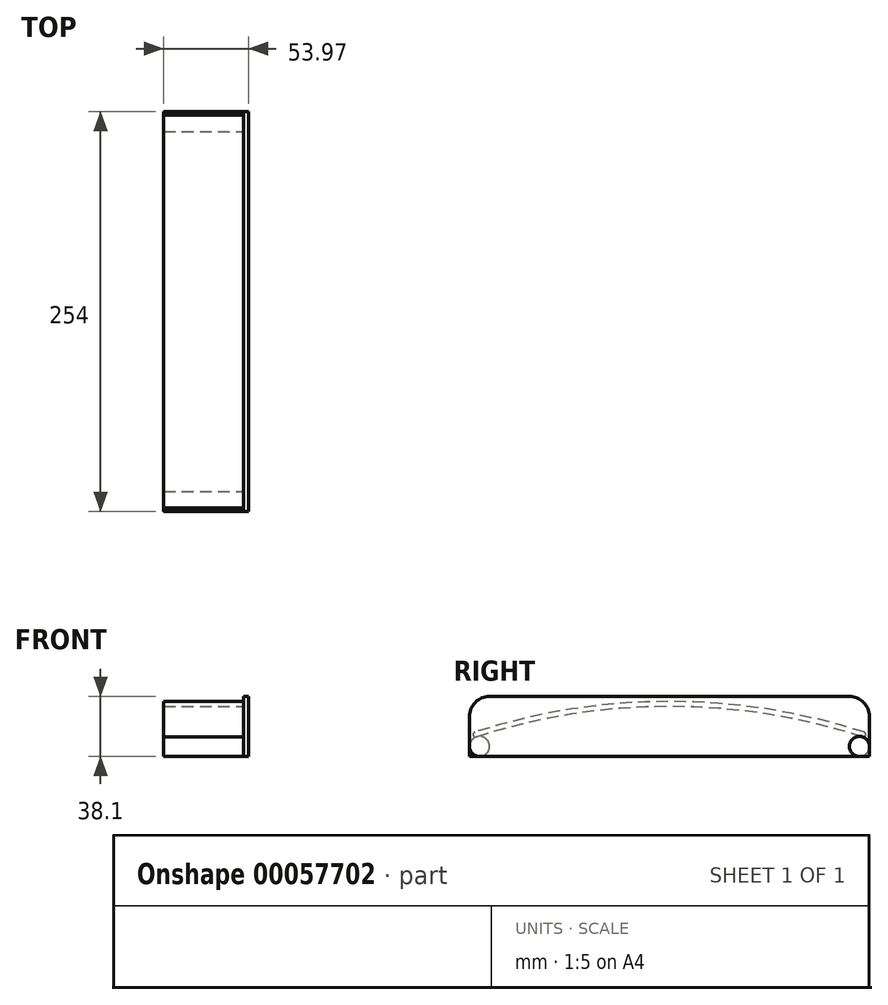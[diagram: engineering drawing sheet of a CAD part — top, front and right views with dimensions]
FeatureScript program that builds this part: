
annotation { "Feature Type Name" : "Feature", "Feature Type Description" : "" }
export const myFeature = defineFeature(function(context is Context, id is Id, definition is map)
    precondition{}
    {
        {
            var Q0;
            Q0=qCreatedBy(makeId("Right.planeOp"),FACE);
            var sketch = newSketch(context, id + "F0", { "sketchPlane" : qUnion([Q0])});
            skLineSegment(sketch, "E0.rect.bottom", {"start": v(-114.3, 19.05) * mm, "end": v(114.3, 19.05) * mm});
            skLineSegment(sketch, "E0.rect.top", {"start": v(-127, -19.05) * mm, "end": v(127, -19.05) * mm});
            skLineSegment(sketch, "E0.rect.left", {"start": v(-127, 6.35) * mm, "end": v(-127, -19.05) * mm});
            skLineSegment(sketch, "E0.rect.right", {"start": v(127, 6.35) * mm, "end": v(127, -19.05) * mm});
            skPoint(sketch, "E0.rect.middle", {"position": v(0, 0) * mm});
            skCircle(sketch, "E1", {"center": v(-120.65, -12.7) * mm, "radius": 6.35 * mm});
            skCircle(sketch, "E2", {"center": v(120.65, -12.7) * mm, "radius": 6.35 * mm});
            skPoint(sketch, "E3.visualSharp", {"position": v(-127, 19.05) * mm});
            skArc(sketch, "E3.filletArc", {"start": v(-114.3, 19.05) * mm, "mid": v(-123.28, 15.33) * mm, "end": v(-127, 6.35) * mm});
            skPoint(sketch, "E4.visualSharp", {"position": v(127, 19.05) * mm});
            skArc(sketch, "E4.filletArc", {"start": v(127, 6.35) * mm, "mid": v(123.28, 15.33) * mm, "end": v(114.3, 19.05) * mm});
            skArc(sketch, "E5", {"start": v(122.6, -6.66) * mm, "mid": v(0, 12.7) * mm, "end": v(-122.6, -6.66) * mm});
            skArc(sketch, "E6.0", {"start": v(123.58, -3.64) * mm, "mid": v(0, 15.87) * mm, "end": v(-123.58, -3.64) * mm});
            skArc(sketch, "E7", {"start": v(-123.58, -3.64) * mm, "mid": v(-124.6, -5.64) * mm, "end": v(-122.6, -6.66) * mm});
            skArc(sketch, "E8", {"start": v(122.6, -6.66) * mm, "mid": v(124.6, -5.64) * mm, "end": v(123.58, -3.64) * mm});
            skSolve(sketch);
        }
        {
            var Q0;
            {var subQ5=sQuery(id+"F0.wireOp",EDGE,"E5");Q0=makeQuery(id+"F0.imprint","IMPRINT",FACE,{"disambiguationData":[TD([[makeQuery(id+"F0.imprint","IMPRINT",EDGE,{"derivedFrom":subQ5}),1.0]])]});}
            var Q1;
            Q1=makeQuery(id+"F0.imprint","IMPRINT",FACE,{"disambiguationData":[TD([[makeQuery(id+"F0.imprint","IMPRINT",EDGE,{"derivedFrom":sQuery(id+"F0.wireOp",EDGE,"E5")}),-1.0]])]});
            var Q2;
            {var subQ0=sQuery(id+"F0.wireOp",EDGE,"E0.rect.left");var subQ1=sQuery(id+"F0.wireOp",EDGE,"E0.rect.top");var subQ2=makeQuery(id+"F0.imprint","INTERSECT",VERTEX,{"derivedFrom":[subQ1,subQ0]});Q2=makeQuery(id+"F0.imprint","IMPRINT",FACE,{"disambiguationData":[TD([[makeQuery(id+"F0.imprint","IMPRINT",EDGE,{"disambiguationData":[TD([[subQ2,-1.0]])],"derivedFrom":subQ1}),1.0]])]});}
            var Q3;
            Q3=makeQuery(id+"F0.imprint","IMPRINT",FACE,{"disambiguationData":[TD([[makeQuery(id+"F0.imprint","IMPRINT",EDGE,{"derivedFrom":sQuery(id+"F0.wireOp",EDGE,"E0.rect.bottom")}),-1.0]])]});
            var Q4;
            {var subQ0=sQuery(id+"F0.wireOp",EDGE,"E0.rect.right");var subQ1=sQuery(id+"F0.wireOp",EDGE,"E0.rect.top");var subQ2=makeQuery(id+"F0.imprint","INTERSECT",VERTEX,{"derivedFrom":[subQ1,subQ0]});Q4=makeQuery(id+"F0.imprint","IMPRINT",FACE,{"disambiguationData":[TD([[makeQuery(id+"F0.imprint","IMPRINT",EDGE,{"disambiguationData":[TD([[subQ2,1.0]])],"derivedFrom":subQ1}),1.0]])]});}
            var Q5;
            {var subQ0=sQuery(id+"F0.wireOp",EDGE,"E1");var subQ3=makeQuery(id+"F0.imprint","INTERSECT",VERTEX,{"derivedFrom":[sQuery(id+"F0.wireOp",EDGE,"E0.rect.top"),subQ0]});Q5=makeQuery(id+"F0.imprint","IMPRINT",FACE,{"disambiguationData":[TD([[makeQuery(id+"F0.imprint","IMPRINT",EDGE,{"disambiguationData":[TD([[subQ3,1.0]])],"derivedFrom":subQ0}),1.0]])]});}
            var Q6;
            {var subQ0=sQuery(id+"F0.wireOp",EDGE,"E2");var subQ3=makeQuery(id+"F0.imprint","INTERSECT",VERTEX,{"derivedFrom":[sQuery(id+"F0.wireOp",EDGE,"E0.rect.top"),subQ0]});Q6=makeQuery(id+"F0.imprint","IMPRINT",FACE,{"disambiguationData":[TD([[makeQuery(id+"F0.imprint","IMPRINT",EDGE,{"disambiguationData":[TD([[subQ3,-1.0]])],"derivedFrom":subQ0}),1.0]])]});}
            extrude(context, id + "F1", {"entities" : qUnion([Q0, Q1, Q2, Q3, Q4, Q5, Q6]), "depth" : 3.17 * mm});
        }
        {
            var Q0;
            {var subQ0=sQuery(id+"F0.wireOp",EDGE,"E1");var subQ3=makeQuery(id+"F0.imprint","INTERSECT",VERTEX,{"derivedFrom":[sQuery(id+"F0.wireOp",EDGE,"E0.rect.top"),subQ0]});Q0=makeQuery(id+"F0.imprint","IMPRINT",FACE,{"disambiguationData":[TD([[makeQuery(id+"F0.imprint","IMPRINT",EDGE,{"disambiguationData":[TD([[subQ3,1.0]])],"derivedFrom":subQ0}),1.0]])]});}
            var Q1;
            {var subQ0=sQuery(id+"F0.wireOp",EDGE,"E2");var subQ3=makeQuery(id+"F0.imprint","INTERSECT",VERTEX,{"derivedFrom":[sQuery(id+"F0.wireOp",EDGE,"E0.rect.top"),subQ0]});Q1=makeQuery(id+"F0.imprint","IMPRINT",FACE,{"disambiguationData":[TD([[makeQuery(id+"F0.imprint","IMPRINT",EDGE,{"disambiguationData":[TD([[subQ3,-1.0]])],"derivedFrom":subQ0}),1.0]])]});}
            extrude(context, id + "F2", {"entities" : qUnion([Q0, Q1]), "oppositeDirection" : true, "depth" : 50.8 * mm});
        }
        {
            var Q0;
            Q0=makeQuery(id+"F0.imprint","IMPRINT",FACE,{"disambiguationData":[TD([[makeQuery(id+"F0.imprint","IMPRINT",EDGE,{"derivedFrom":sQuery(id+"F0.wireOp",EDGE,"E5")}),-1.0]])]});
            var Q1;
            Q1=makeQuery(id+"F2.opExtrude","CAP_FACE",FACE,{"disambiguationData":[OSD([sQuery(id+"F0.wireOp",EDGE,"E2")])],"isStart":false});
            extrude(context, id + "F3", {"entities" : qUnion([Q0]), "endBound" : BoundingType.UP_TO_SURFACE, "oppositeDirection" : true, "endBoundEntityFace" : qUnion([Q1]), "depth" : 25.4 * mm});
        }
    });
